# Revit family: HL_Лючок-прочистка_HL98
name_source: partatom
category: Příslušenství trubek
revit_build: Autodesk Revit 2016 (Build: 20161004_0715(x64)
units: mm (PartAtom-declared; Revit-internal decimal feet)

## family parameters
Kóta kulaté spojky = Použít průměr
Nadpis OmniClass = Liquid Waste Handling Services
Ořezat dutým tvarem při načtení = Ne
Sdílené = Ne
Typ součásti = Normální
Vždy vertikální = Ano
Založené na pracovní rovině = Ne
Číslo OmniClass = 23.70.50.00

## types (1)
- HL98
    Cena = 0 $
    EAN = 9003076701988
    Klíčová poznámka = HL98
    Komentáře k typům = Лючок-прочистка DN110
    Model = HL98
    Popis = Лючок-прочистка DN110
    URL = http://www.hutterer-lechner.com
    Výrobce = HL Hutterer & Lechner GmbH
    ВЕС = 0,838 kg
    МАКСИМАЛЬНАЯ НАГРУЗКА КЛАССА = L 15 - max. 1,5 t
    МАТЕРИАЛ = PP/Edelstahl V2A
    НОМИНАЛЬНЫЙ ДИАМЕТР = 110 mm
    ПРОПУСКНАЯ СПОСОБНОСТЬ = 0.0 m³/h
    РАЗМЕР = DN110
    материал = Plactic - White
    материал 2 = Stainless Steel
